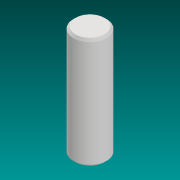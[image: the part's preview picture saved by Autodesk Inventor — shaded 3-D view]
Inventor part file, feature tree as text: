
AUTODESK INVENTOR PART (.ipt)
format: ipt  version: 2021 (Build 250183000, 183)  size: 84,480 bytes
history: native  units: mm
features: other x2, extrude x1, chamfer x1, sketch x1
ambient origin geometry x8: Origin, YZ Plane, XZ Plane, XY Plane, X Axis, Y Axis, Z Axis, Center Point
bodies: 实体1 (feature_tree)
feature tree (5):
  extrude  "拉伸1"  Depth=10.0mm TaperAngle=0.0deg
  chamfer  "倒角1"  Distance=2.0mm Angle=45.0deg
  other  "直接编辑1"
  sketch  "草图1"  dims[d0=30.0mm d1=100.0mm d2=0.0mm d3=2.0mm d4=2.0mm d5=45.0deg d6=4.0mm d7=10.0mm d8=10.0mm]
  other  "缩放比例1"
